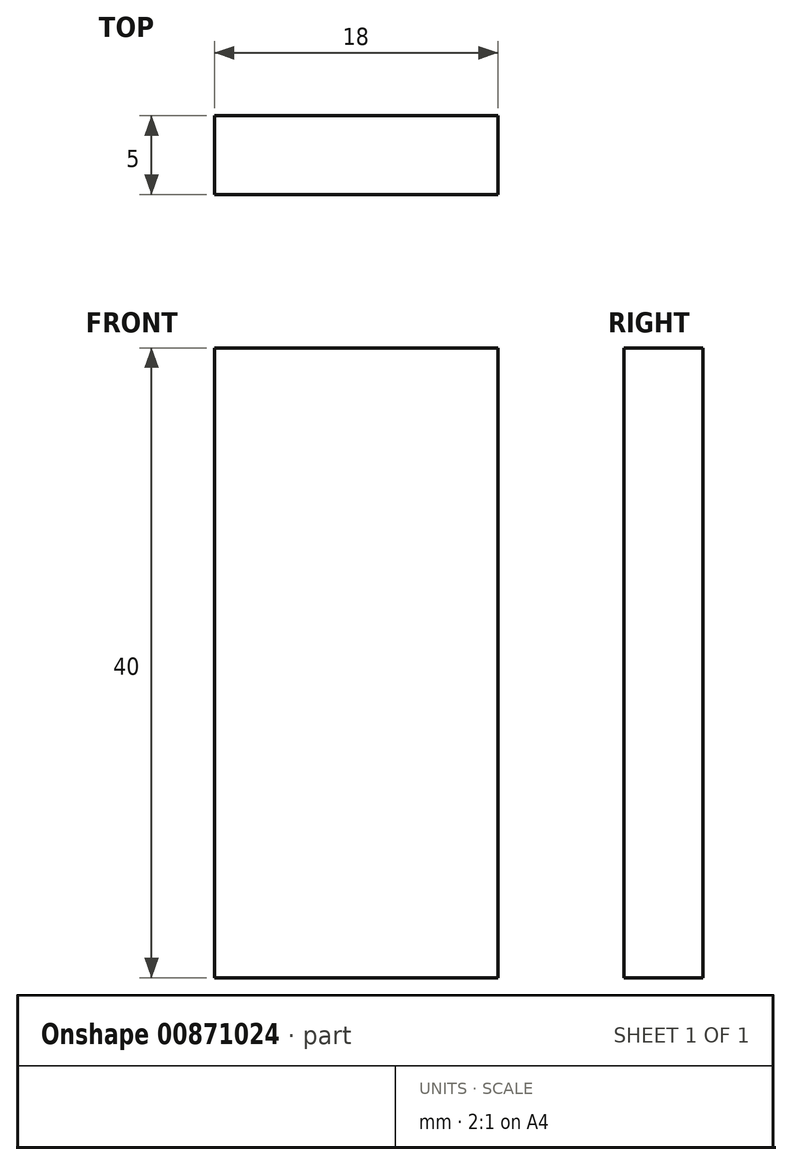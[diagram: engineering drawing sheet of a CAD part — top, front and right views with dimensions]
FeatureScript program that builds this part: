
annotation { "Feature Type Name" : "Feature", "Feature Type Description" : "" }
export const myFeature = defineFeature(function(context is Context, id is Id, definition is map)
    precondition{}
    {
        {
            var Q0;
            Q0=qCreatedBy(makeId("Top.planeOp"),FACE);
            var sketch = newSketch(context, id + "F0", { "sketchPlane" : qUnion([Q0])});
            skLineSegment(sketch, "E0.bottom", {"start": v(-4.1, 1.06) * mm, "end": v(13.9, 1.06) * mm});
            skLineSegment(sketch, "E0.top", {"start": v(-4.1, -3.94) * mm, "end": v(13.9, -3.94) * mm});
            skLineSegment(sketch, "E0.left", {"start": v(-4.1, 1.06) * mm, "end": v(-4.1, -3.94) * mm});
            skLineSegment(sketch, "E0.right", {"start": v(13.9, 1.06) * mm, "end": v(13.9, -3.94) * mm});
            skSolve(sketch);
        }
        {
            var Q0;
            Q0=makeQuery(id+"F0.imprint","IMPRINT",FACE,{"disambiguationData":[TD([[makeQuery(id+"F0.imprint","IMPRINT",EDGE,{"derivedFrom":sQuery(id+"F0.wireOp",EDGE,"E0.bottom")}),-1.0]])]});
            extrude(context, id + "F1", {"entities" : qUnion([Q0]), "depth" : 40 * mm, "offsetDistance" : 25 * mm});
        }
    });
